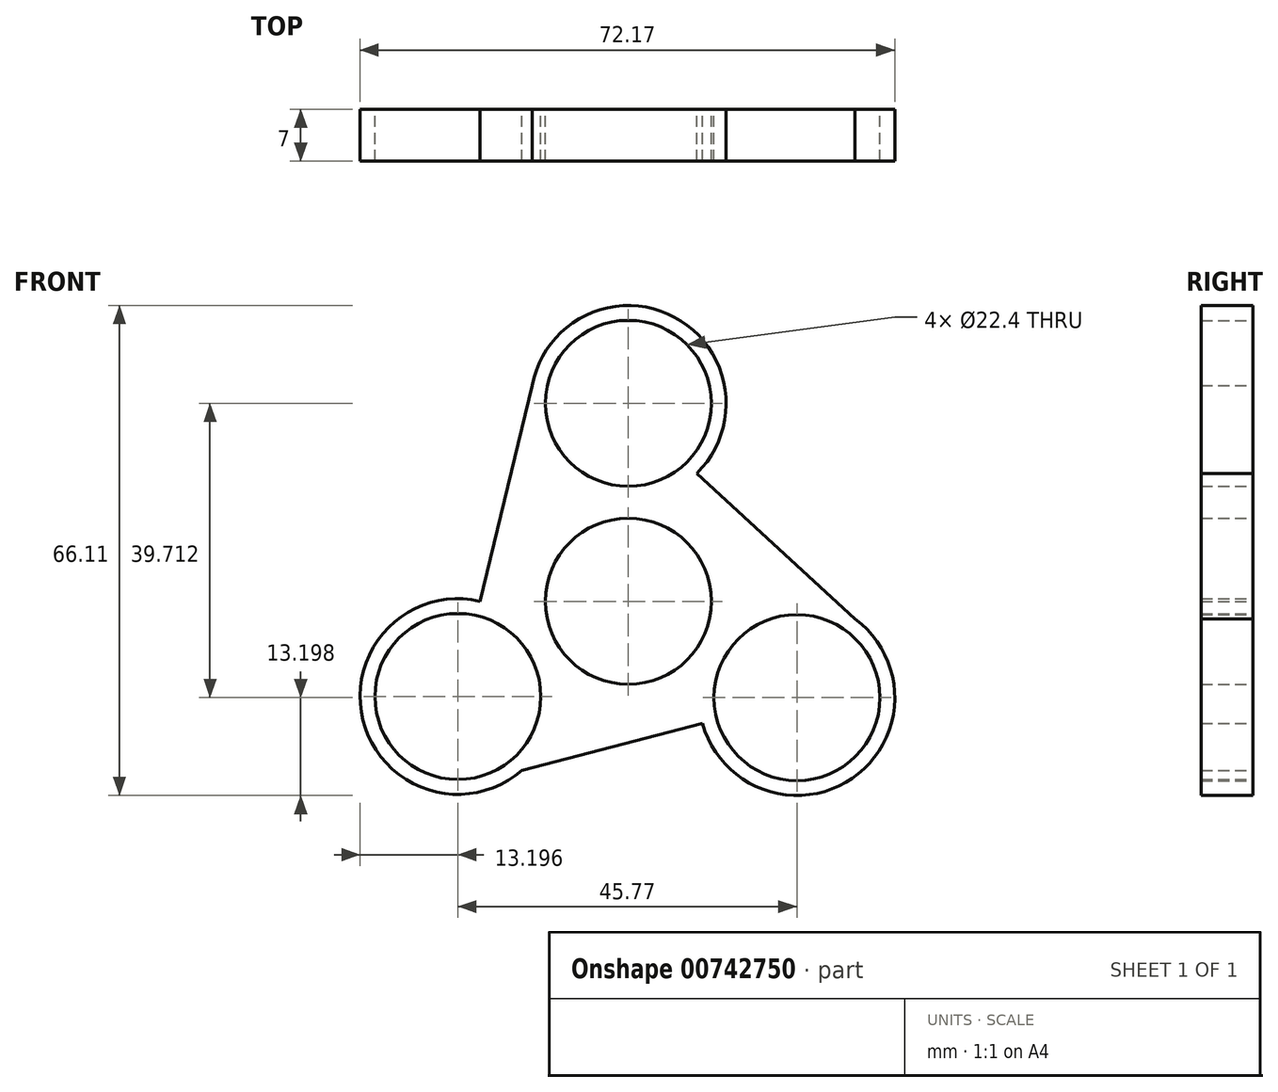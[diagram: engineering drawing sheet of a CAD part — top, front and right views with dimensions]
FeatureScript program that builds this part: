
annotation { "Feature Type Name" : "Feature", "Feature Type Description" : "" }
export const myFeature = defineFeature(function(context is Context, id is Id, definition is map)
    precondition{}
    {
        {
            var Q0;
            Q0=qCreatedBy(makeId("Front.planeOp"),FACE);
            var sketch = newSketch(context, id + "F0", { "sketchPlane" : qUnion([Q0])});
            skCircle(sketch, "E0", {"center": v(0, 0) * mm, "radius": 11.2 * mm});
            skCircle(sketch, "E1", {"center": v(0, 26.71) * mm, "radius": 11.2 * mm});
            skArc(sketch, "E2", {"start": v(9.23, 17.27) * mm, "mid": v(6.22, 38.35) * mm, "end": v(-12.97, 29.15) * mm});
            skCircle(sketch, "E3.1.0", {"center": v(-23.01, -12.85) * mm, "radius": 11.2 * mm});
            skCircle(sketch, "E3.2.0", {"center": v(22.76, -13) * mm, "radius": 11.2 * mm});
            skArc(sketch, "E3.2.1", {"start": v(10.03, -16.5) * mm, "mid": v(30.22, -23.9) * mm, "end": v(30.6, -2.4) * mm});
            skPoint(sketch, "E3.center", {"position": v(-0.09, 0.28) * mm});
            skPoint(sketch, "E4.end.orphan", {"position": v(-20, 0) * mm});
            skLineSegment(sketch, "E5", {"start": v(-12.97, 29.15) * mm, "end": v(-20, 0) * mm});
            skLineSegment(sketch, "E6", {"start": v(-14.37, -22.83) * mm, "end": v(10.03, -16.5) * mm});
            skLineSegment(sketch, "E7", {"start": v(30.6, -2.4) * mm, "end": v(9.23, 17.27) * mm});
            skArc(sketch, "E8.trimOffspring", {"start": v(-20, 0) * mm, "mid": v(-35.83, -16.01) * mm, "end": v(-14.37, -22.83) * mm});
            skSolve(sketch);
        }
        {
            var Q0;
            Q0=makeQuery(id+"F0.imprint","IMPRINT",FACE,{"disambiguationData":[TD([[makeQuery(id+"F0.imprint","IMPRINT",EDGE,{"derivedFrom":sQuery(id+"F0.wireOp",EDGE,"E0")}),-1.0]])]});
            extrude(context, id + "F1", {"entities" : qUnion([Q0]), "depth" : 7 * mm, "offsetDistance" : 25 * mm});
        }
    });
